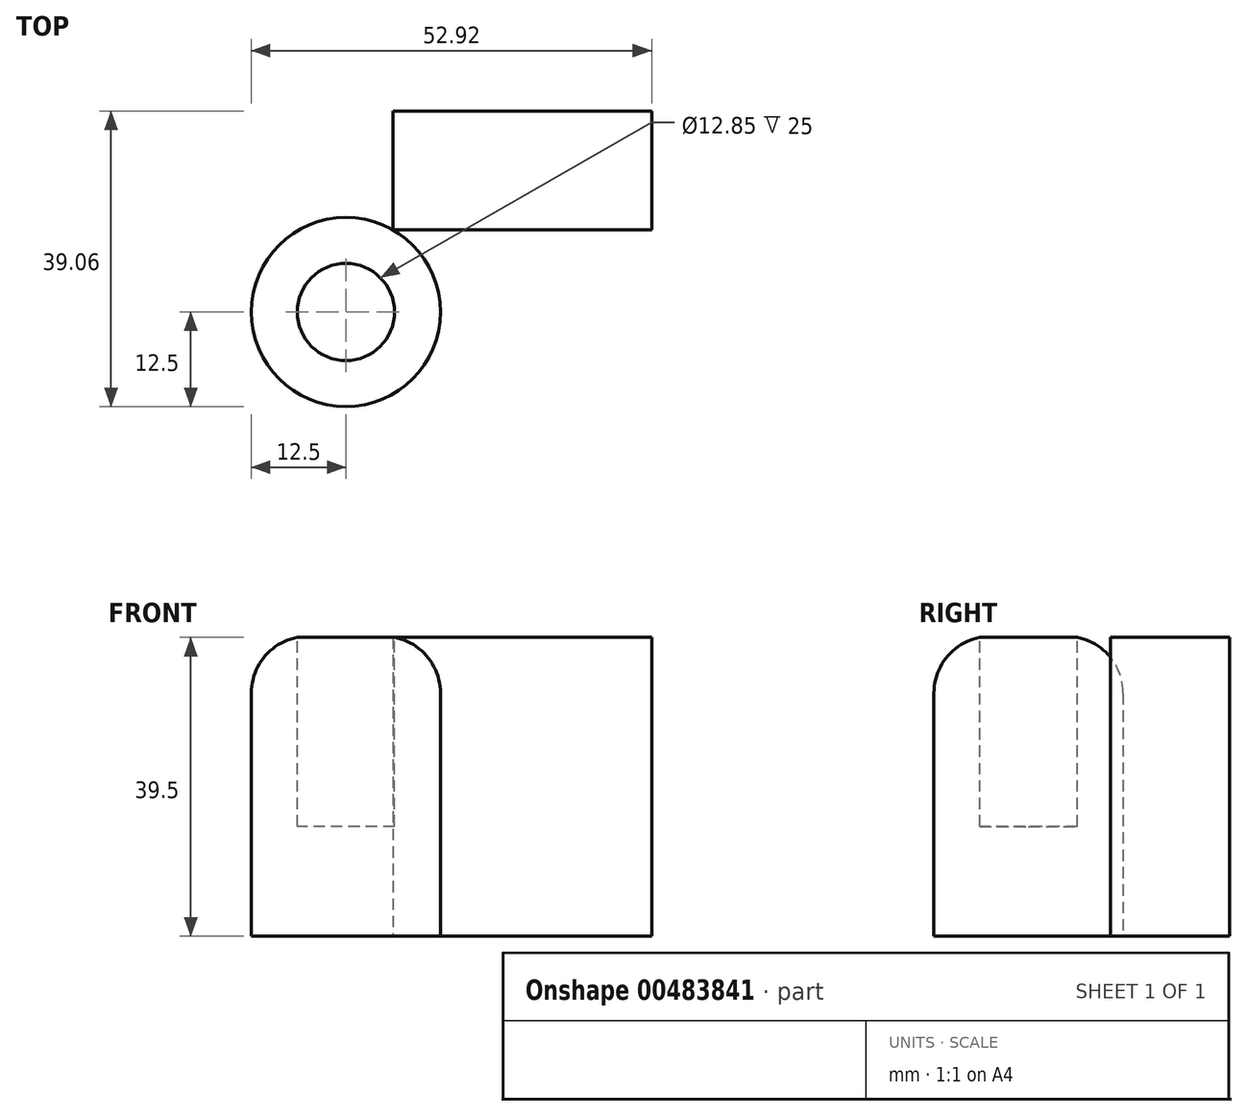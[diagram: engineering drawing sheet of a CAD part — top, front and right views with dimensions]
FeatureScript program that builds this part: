
annotation { "Feature Type Name" : "Feature", "Feature Type Description" : "" }
export const myFeature = defineFeature(function(context is Context, id is Id, definition is map)
    precondition{}
    {
        {
            var Q0;
            Q0=qCreatedBy(makeId("Top.planeOp"),FACE);
            var sketch = newSketch(context, id + "F0", { "sketchPlane" : qUnion([Q0])});
            skCircle(sketch, "E0", {"center": v(0, 0) * mm, "radius": 12.5 * mm});
            skLineSegment(sketch, "E1.bottom", {"start": v(6.21, 10.85) * mm, "end": v(40.42, 10.85) * mm});
            skLineSegment(sketch, "E1.top", {"start": v(6.21, 26.56) * mm, "end": v(40.42, 26.56) * mm});
            skLineSegment(sketch, "E1.left", {"start": v(6.21, 10.85) * mm, "end": v(6.21, 26.56) * mm});
            skLineSegment(sketch, "E1.right", {"start": v(40.42, 10.85) * mm, "end": v(40.42, 26.56) * mm});
            skSolve(sketch);
        }
        {
            var Q0;
            Q0 = qSketchRegion(id + "F0", true);
            extrude(context, id + "F1", {"entities" : qUnion([Q0]), "depth" : 39.5 * mm});
        }
        {
            var Q0;
            Q0=makeQuery(id+"F1.opExtrude","CAP_FACE",FACE,{"disambiguationData":[OSD([sQuery(id+"F0.wireOp",EDGE,"E0")])],"isStart":false});
            var sketch = newSketch(context, id + "F2", { "sketchPlane" : qUnion([Q0])});
            skCircle(sketch, "E2", {"center": v(0, 0) * mm, "radius": 6.42 * mm});
            skSolve(sketch);
        }
        {
            var Q0;
            Q0 = qSketchRegion(id + "F2", true);
            extrude(context, id + "F3", {"entities" : qUnion([Q0]), "operationType" : NewBodyOperationType.REMOVE, "oppositeDirection" : true, "depth" : 25 * mm});
        }
        {
            var Q0;
            Q0=makeQuery(id+"F1.opExtrude","CAP_EDGE",EDGE,{"disambiguationData":[OSD([sQuery(id+"F0.wireOp",EDGE,"E0")])],"isStart":false});
            fillet(context, id + "F4", {"entities" : qUnion([Q0]), "radius" : 7.48 * mm, "tangentPropagation" : true, "allowEdgeOverflow" : false});
        }
    });
